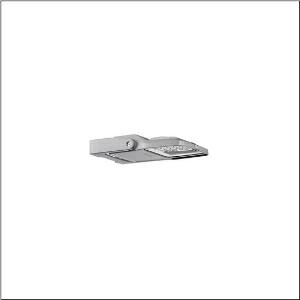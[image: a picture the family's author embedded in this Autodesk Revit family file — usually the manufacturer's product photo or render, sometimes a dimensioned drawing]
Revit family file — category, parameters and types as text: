
# Revit family: floodlight_fl_21_iq_micro___pl64_5xa7762a2e2a_90eb
name_source: partatom
category: Lighting Fixtures
units: mm (PartAtom-declared; Revit-internal decimal feet)

## family parameters
Cut with Voids When Loaded = No
Host = Face
Light Source = No
Part Type = Normal
Room Calculation Point = No
Round Connector Dimension = Use Diameter
Shared = No

## types (1)
- --- (1 x LED, 2870 lm, 23.1 W, 3000K)
    Apparent Load = 23 VA
    CIE Flux Codes = 28 80 98 100 100
    Color Rendering = 70
    Color Temperature = 3000K
    Default Elevation = 1800 mm
    Description = Floodlight FL 21 iQ micro, floodlight, primary light control with lens, of PMMA, primary optical cover: protective disc, of toughened safety glass, transparent, light distribution: PL64, light emission: direct distribution, installation type: surface-mounted, LED, High Power LED, rated luminous flux: 2.870lm, luminous efficacy: 124lm/W, light colour: 730, colour temperature: 3000K, control: Auto-Match, Temp-Guard, Night-Set, Smart-Wire, Desk-Remote (wireless, voltage-free reading and setting of iQ features in the workshop via application-optimized NFC function/RFID function), optimised constant luminous flux control (CLO 2.0), Street-Remote, with terminal, 6-pole, mains connection: 220..240V, AC, 50/60Hz, start of lifetime: 23W, end of service life: 24W, reduction: 11W, luminaire housing, of diecast aluminium, powder-coated, Siteco® metallic grey (DB 702S), corrosivity category C5 mid according to DIN EN ISO 12944, sealing non-destructively replaceable, design bracket, of diecast aluminium, powder-coated, Siteco® metallic grey (DB 702S), protection rating (complete): IP66, insulation class (complete): insulation class II (safety insulation), certification: CE, ENEC, VDE, protection symbol: D, impact resistance: IK07, permissible operating ambient temperature: -40..+40°C, permissible operating ambient temperature for outdoor applications: -40..+50°C, standard: DIN EN 12944, LABS conformity tested according to VDMA 24364:2018-05, packaging unit: 1 piece

Light Distribution: PL64
    Height = 65 mm
    Lamp = 1 x LED
    Lamp Light Flux = 2870 lm
    Lamp Power = 23.1 W
    Lamp count = 1
    Length = 312 mm
    Luminous efficacy = 124 lm/W
    Manufacturer = Siteco
    ModVariant = No
    Model = 5XA7762A2E2A
    Mounting Place = Wall
    Mounting Type = Surface mounted
    Number of Poles = 1
    OnlyDefault = Yes
    Power Factor = 1
    Product Name = Floodlight FL 21 iQ micro | PL64
    Product group = floodlight | wall mounted
    ProductGroupID = 2001
    Protection Class = Protection class II
    Protection Degree = IP 66
    RLX_Detail_Level = 1
    RLX_Emergency_Light_Flux = 0 lm
    RLX_Emergency_Type = 0
    RLX_Emergency_Type_DB = No
    RlxData = <blob elided: 97437 chars, md5=427318ff>
    Socket = socket
    Standby Power = 0 W
    System Light Flux = 2870 lm
    System Power = 23 W
    Type Comments = factory setting: luminous flux: 100 % | dim-lin: 254 | 455 mA
    Type Image = l_1006878.jpg
    URL = http://relux.com
    VarID = @adj_152151
    Voltage = 0 V
    Weight = 0.00 kg
    Width = 230 mm

## geometry (parser evidence)
native form markers: Blend x4, Sweep x13
no freeform markers — native parametric forms only
